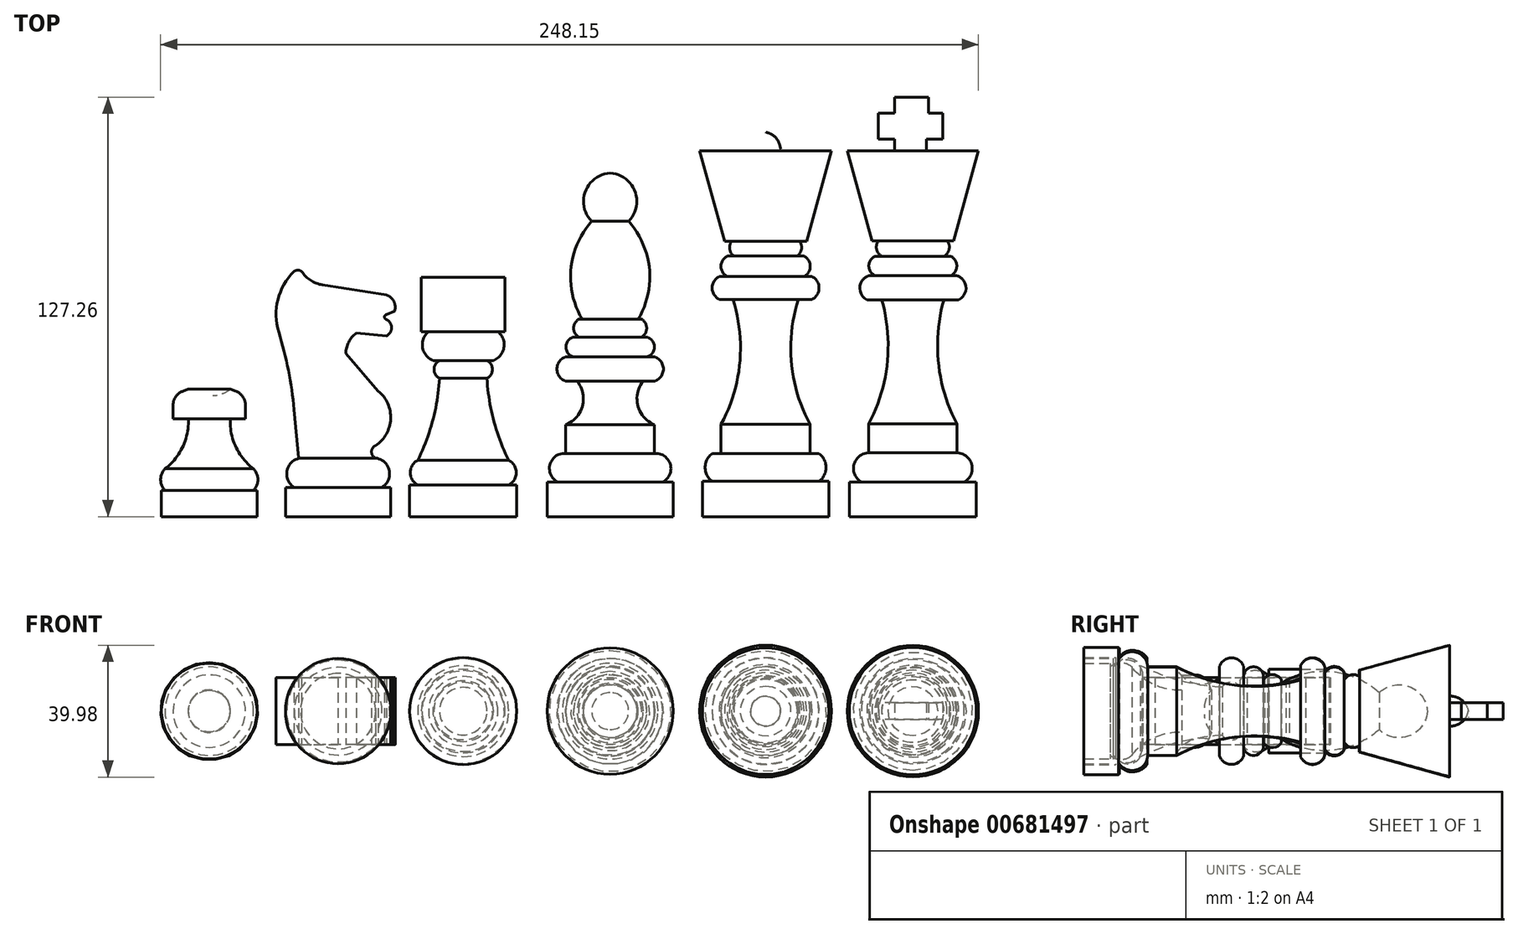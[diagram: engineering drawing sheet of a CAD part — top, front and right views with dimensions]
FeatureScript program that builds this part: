
annotation { "Feature Type Name" : "Feature", "Feature Type Description" : "" }
export const myFeature = defineFeature(function(context is Context, id is Id, definition is map)
    precondition{}
    {
        {
            var Q0;
            Q0=qCreatedBy(makeId("Top.planeOp"),FACE);
            var sketch = newSketch(context, id + "F0", { "sketchPlane" : qUnion([Q0])});
            skLineSegment(sketch, "E0", {"start": v(0, 0) * mm, "end": v(0, 127.26) * mm});
            skLineSegment(sketch, "E1", {"start": v(0, 0) * mm, "end": v(19.3, 0) * mm});
            skLineSegment(sketch, "E2", {"start": v(19.3, 0) * mm, "end": v(19.3, 10.5) * mm});
            skLineSegment(sketch, "E3", {"start": v(19.3, 10.5) * mm, "end": v(15.6, 10.5) * mm});
            skLineSegment(sketch, "E4", {"start": v(13.4, 19.39) * mm, "end": v(13.4, 28.12) * mm});
            skArc(sketch, "E5", {"start": v(9.43, 65.79) * mm, "mid": v(7.78, 46.57) * mm, "end": v(13.4, 28.12) * mm});
            skLineSegment(sketch, "E6", {"start": v(9.43, 65.79) * mm, "end": v(13.93, 65.79) * mm});
            skArc(sketch, "E7", {"start": v(13.93, 65.79) * mm, "mid": v(16.1, 69.74) * mm, "end": v(13.14, 73.14) * mm});
            skLineSegment(sketch, "E8", {"start": v(13.14, 73.14) * mm, "end": v(11.52, 73.14) * mm});
            skArc(sketch, "E9", {"start": v(11.52, 73.14) * mm, "mid": v(13.36, 76.06) * mm, "end": v(11.52, 78.98) * mm});
            skLineSegment(sketch, "E10", {"start": v(11.52, 78.98) * mm, "end": v(9.46, 78.98) * mm});
            skArc(sketch, "E11", {"start": v(9.46, 78.98) * mm, "mid": v(11.01, 81.12) * mm, "end": v(10.4, 83.7) * mm});
            skLineSegment(sketch, "E12", {"start": v(10.4, 83.7) * mm, "end": v(12.4, 83.7) * mm});
            skLineSegment(sketch, "E13", {"start": v(12.4, 83.7) * mm, "end": v(19.92, 110.96) * mm});
            skLineSegment(sketch, "E14", {"start": v(4.77, 127.26) * mm, "end": v(-5.47, 127.26) * mm});
            skLineSegment(sketch, "E15", {"start": v(19.92, 110.96) * mm, "end": v(0, 110.96) * mm});
            skArc(sketch, "E16", {"start": v(15.6, 10.5) * mm, "mid": v(17.9, 15.67) * mm, "end": v(13.6, 19.37) * mm});
            skLineSegment(sketch, "E17", {"start": v(13.4, 19.39) * mm, "end": v(13.6, 19.37) * mm});
            skLineSegment(sketch, "E18", {"start": v(0, 110.96) * mm, "end": v(0, 0) * mm});
            skLineSegment(sketch, "E19", {"start": v(0, 110.96) * mm, "end": v(0, 127.26) * mm});
            skLineSegment(sketch, "E20", {"start": v(4.77, 127.26) * mm, "end": v(4.77, 122.37) * mm});
            skLineSegment(sketch, "E21", {"start": v(4.77, 122.37) * mm, "end": v(9.1, 122.37) * mm});
            skLineSegment(sketch, "E22", {"start": v(9.1, 122.37) * mm, "end": v(9.1, 114.55) * mm});
            skLineSegment(sketch, "E23", {"start": v(9.1, 114.55) * mm, "end": v(4.14, 114.55) * mm});
            skLineSegment(sketch, "E24", {"start": v(4.14, 114.55) * mm, "end": v(4.14, 110.96) * mm});
            skLineSegment(sketch, "E25", {"start": v(-5.47, 127.26) * mm, "end": v(-5.47, 122.37) * mm});
            skLineSegment(sketch, "E26", {"start": v(-5.47, 122.37) * mm, "end": v(-10.42, 122.37) * mm});
            skLineSegment(sketch, "E27", {"start": v(-10.42, 122.37) * mm, "end": v(-10.42, 114.55) * mm});
            skLineSegment(sketch, "E28", {"start": v(-10.42, 114.55) * mm, "end": v(-5.47, 114.55) * mm});
            skLineSegment(sketch, "E29", {"start": v(-5.47, 114.55) * mm, "end": v(-5.47, 110.96) * mm});
            skLineSegment(sketch, "E30", {"start": v(-5.47, 110.96) * mm, "end": v(0, 110.96) * mm});
            skLineSegment(sketch, "E31", {"start": v(-44.68, 0) * mm, "end": v(-25.47, 0) * mm});
            skLineSegment(sketch, "E32", {"start": v(-25.47, 0) * mm, "end": v(-25.47, 10.69) * mm});
            skLineSegment(sketch, "E33", {"start": v(-25.47, 10.69) * mm, "end": v(-28.51, 10.69) * mm});
            skArc(sketch, "E34", {"start": v(-28.51, 10.69) * mm, "mid": v(-26.34, 14.92) * mm, "end": v(-28.51, 19.15) * mm});
            skLineSegment(sketch, "E35", {"start": v(-28.51, 19.15) * mm, "end": v(-31.18, 19.15) * mm});
            skLineSegment(sketch, "E36", {"start": v(-31.18, 19.15) * mm, "end": v(-31.18, 28.02) * mm});
            skArc(sketch, "E37", {"start": v(-34.78, 65.9) * mm, "mid": v(-36.84, 46.6) * mm, "end": v(-31.18, 28.02) * mm});
            skLineSegment(sketch, "E38", {"start": v(-34.78, 65.9) * mm, "end": v(-30.58, 65.9) * mm});
            skArc(sketch, "E39", {"start": v(-30.58, 65.9) * mm, "mid": v(-28.47, 69.37) * mm, "end": v(-30.58, 72.84) * mm});
            skLineSegment(sketch, "E40", {"start": v(-30.58, 72.84) * mm, "end": v(-33.03, 72.84) * mm});
            skArc(sketch, "E41", {"start": v(-33.03, 72.84) * mm, "mid": v(-31.13, 75.93) * mm, "end": v(-33.03, 79.02) * mm});
            skLineSegment(sketch, "E42", {"start": v(-33.03, 79.02) * mm, "end": v(-35.05, 79.02) * mm});
            skArc(sketch, "E43", {"start": v(-35.05, 79.02) * mm, "mid": v(-33.8, 81.1) * mm, "end": v(-34.32, 83.47) * mm});
            skLineSegment(sketch, "E44", {"start": v(-34.32, 83.47) * mm, "end": v(-32.26, 83.47) * mm});
            skLineSegment(sketch, "E45", {"start": v(-32.26, 83.47) * mm, "end": v(-24.7, 110.92) * mm});
            skLineSegment(sketch, "E46", {"start": v(-24.7, 110.92) * mm, "end": v(-44.68, 110.92) * mm});
            skLineSegment(sketch, "E47", {"start": v(-44.68, 110.92) * mm, "end": v(-44.68, 0) * mm});
            skLineSegment(sketch, "E48", {"start": v(-44.68, 110.92) * mm, "end": v(-44.68, 116.61) * mm});
            skArc(sketch, "E49", {"start": v(-40.14, 110.92) * mm, "mid": v(-41.33, 114.62) * mm, "end": v(-44.68, 116.61) * mm});
            skLineSegment(sketch, "E50", {"start": v(-91.84, 0) * mm, "end": v(-72.7, 0) * mm});
            skLineSegment(sketch, "E51", {"start": v(-72.7, 0) * mm, "end": v(-72.7, 10.5) * mm});
            skLineSegment(sketch, "E52", {"start": v(-72.7, 10.5) * mm, "end": v(-75.93, 10.5) * mm});
            skArc(sketch, "E53", {"start": v(-75.93, 10.5) * mm, "mid": v(-73.47, 15.34) * mm, "end": v(-77.33, 19.15) * mm});
            skLineSegment(sketch, "E54", {"start": v(-77.33, 19.15) * mm, "end": v(-78.38, 19.15) * mm});
            skLineSegment(sketch, "E55", {"start": v(-78.38, 19.15) * mm, "end": v(-78.38, 27.88) * mm});
            skArc(sketch, "E56", {"start": v(-81.78, 41.15) * mm, "mid": v(-83.44, 33.65) * mm, "end": v(-78.38, 27.88) * mm});
            skLineSegment(sketch, "E57", {"start": v(-81.78, 41.15) * mm, "end": v(-78.22, 41.15) * mm});
            skArc(sketch, "E58", {"start": v(-78.22, 41.15) * mm, "mid": v(-75.7, 44.8) * mm, "end": v(-78.22, 48.43) * mm});
            skLineSegment(sketch, "E59", {"start": v(-78.22, 48.43) * mm, "end": v(-80.75, 48.43) * mm});
            skArc(sketch, "E60", {"start": v(-80.75, 48.43) * mm, "mid": v(-78.41, 51.46) * mm, "end": v(-80.75, 54.48) * mm});
            skLineSegment(sketch, "E61", {"start": v(-80.75, 54.48) * mm, "end": v(-82.28, 54.48) * mm});
            skArc(sketch, "E62", {"start": v(-82.28, 54.48) * mm, "mid": v(-80.76, 57.18) * mm, "end": v(-82.28, 59.87) * mm});
            skLineSegment(sketch, "E63", {"start": v(-82.28, 59.87) * mm, "end": v(-83.35, 59.87) * mm});
            skArc(sketch, "E64", {"start": v(-83.35, 59.87) * mm, "mid": v(-79.94, 75.2) * mm, "end": v(-86.24, 89.57) * mm});
            skArc(sketch, "E65", {"start": v(-86.24, 89.57) * mm, "mid": v(-84.33, 98.68) * mm, "end": v(-91.84, 104.19) * mm});
            skLineSegment(sketch, "E66", {"start": v(-91.84, 104.19) * mm, "end": v(-91.84, 0) * mm});
            skLineSegment(sketch, "E67", {"start": v(-136.43, 0) * mm, "end": v(-120.2, 0) * mm});
            skLineSegment(sketch, "E68", {"start": v(-120.2, 0) * mm, "end": v(-120.2, 9.62) * mm});
            skLineSegment(sketch, "E69", {"start": v(-120.2, 9.62) * mm, "end": v(-122.64, 9.62) * mm});
            skArc(sketch, "E70", {"start": v(-122.64, 9.62) * mm, "mid": v(-120.34, 13.36) * mm, "end": v(-122.64, 17.1) * mm});
            skArc(sketch, "E71", {"start": v(-129.21, 41.96) * mm, "mid": v(-127.2, 29.2) * mm, "end": v(-122.64, 17.1) * mm});
            skArc(sketch, "E72", {"start": v(-129.21, 41.96) * mm, "mid": v(-127.57, 44.66) * mm, "end": v(-129.21, 47.37) * mm});
            skLineSegment(sketch, "E73", {"start": v(-129.21, 47.37) * mm, "end": v(-127.23, 47.37) * mm});
            skArc(sketch, "E74", {"start": v(-127.23, 47.37) * mm, "mid": v(-124.06, 51.37) * mm, "end": v(-125.93, 56.12) * mm});
            skLineSegment(sketch, "E75", {"start": v(-125.93, 56.12) * mm, "end": v(-123.74, 56.12) * mm});
            skLineSegment(sketch, "E76", {"start": v(-123.74, 56.12) * mm, "end": v(-123.74, 72.64) * mm});
            skLineSegment(sketch, "E77", {"start": v(-123.74, 72.64) * mm, "end": v(-136.43, 72.64) * mm});
            skLineSegment(sketch, "E78", {"start": v(-136.43, 72.64) * mm, "end": v(-136.43, 0) * mm});
            skLineSegment(sketch, "E79", {"start": v(-213.48, 0) * mm, "end": v(-199, 0) * mm});
            skLineSegment(sketch, "E80", {"start": v(-199, 0) * mm, "end": v(-199, 7.95) * mm});
            skLineSegment(sketch, "E81", {"start": v(-199, 7.95) * mm, "end": v(-200.07, 7.95) * mm});
            skArc(sketch, "E82", {"start": v(-200.07, 7.95) * mm, "mid": v(-198.73, 11.23) * mm, "end": v(-200.07, 14.51) * mm});
            skArc(sketch, "E83", {"start": v(-207.12, 29.7) * mm, "mid": v(-205.47, 21.24) * mm, "end": v(-200.07, 14.51) * mm});
            skLineSegment(sketch, "E84", {"start": v(-207.12, 29.7) * mm, "end": v(-202.5, 29.7) * mm});
            skLineSegment(sketch, "E85", {"start": v(-202.5, 29.7) * mm, "end": v(-202.5, 33.78) * mm});
            skArc(sketch, "E86", {"start": v(-202.5, 33.78) * mm, "mid": v(-203.31, 36.39) * mm, "end": v(-205.47, 38.07) * mm});
            skLineSegment(sketch, "E87", {"start": v(-205.47, 38.07) * mm, "end": v(-207.05, 38.66) * mm});
            skArc(sketch, "E88", {"start": v(-207.05, 38.66) * mm, "mid": v(-204.14, 49.4) * mm, "end": v(-213.48, 55.46) * mm});
            skLineSegment(sketch, "E89", {"start": v(-213.48, 55.46) * mm, "end": v(-213.48, 0) * mm});
            skLineSegment(sketch, "E90", {"start": v(-174.39, 0) * mm, "end": v(-158.4, 0) * mm});
            skLineSegment(sketch, "E91", {"start": v(-158.4, 0) * mm, "end": v(-158.4, 8.9) * mm});
            skLineSegment(sketch, "E92", {"start": v(-158.4, 8.9) * mm, "end": v(-161.1, 8.9) * mm});
            skArc(sketch, "E93", {"start": v(-161.1, 8.9) * mm, "mid": v(-158.89, 14) * mm, "end": v(-162.97, 17.77) * mm});
            skLineSegment(sketch, "E94", {"start": v(-162.97, 17.77) * mm, "end": v(-174.39, 17.77) * mm});
            skLineSegment(sketch, "E95", {"start": v(-174.39, 17.77) * mm, "end": v(-174.39, 0) * mm});
            skArc(sketch, "E96", {"start": v(-162.97, 21.59) * mm, "mid": v(-164.25, 19.68) * mm, "end": v(-162.97, 17.77) * mm});
            skArc(sketch, "E97", {"start": v(-162.97, 21.59) * mm, "mid": v(-158.46, 29.65) * mm, "end": v(-162.2, 38.1) * mm});
            skLineSegment(sketch, "E98", {"start": v(-162.2, 38.1) * mm, "end": v(-172.04, 49.47) * mm});
            skArc(sketch, "E99", {"start": v(-168.89, 55.65) * mm, "mid": v(-171.2, 52.93) * mm, "end": v(-172.04, 49.47) * mm});
            skLineSegment(sketch, "E100", {"start": v(-168.89, 55.65) * mm, "end": v(-159.67, 54.86) * mm});
            skArc(sketch, "E101", {"start": v(-159.67, 54.86) * mm, "mid": v(-158.17, 57.31) * mm, "end": v(-159.67, 59.76) * mm});
            skArc(sketch, "E102", {"start": v(-159.67, 61.33) * mm, "mid": v(-160.33, 60.55) * mm, "end": v(-159.67, 59.76) * mm});
            skLineSegment(sketch, "E103", {"start": v(-159.67, 61.33) * mm, "end": v(-157.26, 62.3) * mm});
            skArc(sketch, "E104", {"start": v(-157.26, 62.3) * mm, "mid": v(-157.47, 65.3) * mm, "end": v(-159.75, 67.24) * mm});
            skLineSegment(sketch, "E105", {"start": v(-159.75, 67.24) * mm, "end": v(-179.11, 70.29) * mm});
            skArc(sketch, "E106", {"start": v(-185.45, 74.34) * mm, "mid": v(-182.7, 71.65) * mm, "end": v(-179.11, 70.29) * mm});
            skArc(sketch, "E107", {"start": v(-185.45, 74.34) * mm, "mid": v(-186.6, 74.76) * mm, "end": v(-187.73, 74.34) * mm});
            skArc(sketch, "E108", {"start": v(-187.73, 74.34) * mm, "mid": v(-192.67, 65.82) * mm, "end": v(-192.4, 55.97) * mm});
            skArc(sketch, "E109", {"start": v(-187.73, 32.46) * mm, "mid": v(-189.45, 44.34) * mm, "end": v(-192.4, 55.97) * mm});
            skLineSegment(sketch, "E110", {"start": v(-187.73, 32.46) * mm, "end": v(-186.4, 17.8) * mm});
            skLineSegment(sketch, "E111", {"start": v(-186.4, 17.8) * mm, "end": v(-174.39, 17.77) * mm});
            skSolve(sketch);
        }
        {
            var Q0;
            {var subQ0=sQuery(id+"F0.wireOp",EDGE,"E1");Q0=makeQuery(id+"F0.imprint","IMPRINT",FACE,{"disambiguationData":[TD([[makeQuery(id+"F0.imprint","IMPRINT",EDGE,{"derivedFrom":subQ0}),1.0]])]});}
            var Q1;
            Q1=sQuery(id+"F0.wireOp",EDGE,"E0");
            revolve(context, id + "F1", {"entities" : qUnion([Q0]), "axis" : qUnion([Q1]), "revolveType" : RevolveType.FULL});
        }
        {
            var Q0;
            {var subQ3=sQuery(id+"F0.wireOp",EDGE,"E25");Q0=makeQuery(id+"F0.imprint","IMPRINT",FACE,{"disambiguationData":[TD([[makeQuery(id+"F0.imprint","IMPRINT",EDGE,{"derivedFrom":subQ3}),1.0]])]});}
            var Q1;
            {var subQ4=sQuery(id+"F0.wireOp",EDGE,"E20");Q1=makeQuery(id+"F0.imprint","IMPRINT",FACE,{"disambiguationData":[TD([[makeQuery(id+"F0.imprint","IMPRINT",EDGE,{"derivedFrom":subQ4}),-1.0]])]});}
            extrude(context, id + "F2", {"entities" : qUnion([Q0, Q1]), "operationType" : NewBodyOperationType.ADD, "endBound" : BoundingType.SYMMETRIC, "depth" : 5.08 * mm, "offsetDistance" : 25.4 * mm});
        }
        {
            var Q0;
            Q0=makeQuery(id+"F0.imprint","IMPRINT",FACE,{"disambiguationData":[TD([[makeQuery(id+"F0.imprint","IMPRINT",EDGE,{"derivedFrom":sQuery(id+"F0.wireOp",EDGE,"E31")}),1.0]])]});
            var Q1;
            Q1=sQuery(id+"F0.wireOp",EDGE,"E47");
            revolve(context, id + "F3", {"entities" : qUnion([Q0]), "axis" : qUnion([Q1]), "revolveType" : RevolveType.FULL});
        }
        {
            var Q0;
            {var subQ0=sQuery(id+"F0.wireOp",EDGE,"E48");Q0=makeQuery(id+"F0.imprint","IMPRINT",FACE,{"disambiguationData":[TD([[makeQuery(id+"F0.imprint","IMPRINT",EDGE,{"derivedFrom":subQ0}),-1.0]])]});}
            var Q1;
            Q1=sQuery(id+"F0.wireOp",EDGE,"E48");
            revolve(context, id + "F4", {"operationType" : NewBodyOperationType.ADD, "entities" : qUnion([Q0]), "axis" : qUnion([Q1]), "revolveType" : RevolveType.FULL});
        }
        {
            var Q0;
            Q0=makeQuery(id+"F0.imprint","IMPRINT",FACE,{"disambiguationData":[TD([[makeQuery(id+"F0.imprint","IMPRINT",EDGE,{"derivedFrom":sQuery(id+"F0.wireOp",EDGE,"E50")}),1.0]])]});
            var Q1;
            Q1=sQuery(id+"F0.wireOp",EDGE,"E66");
            revolve(context, id + "F5", {"entities" : qUnion([Q0]), "axis" : qUnion([Q1]), "revolveType" : RevolveType.FULL});
        }
        {
            var Q0;
            Q0=makeQuery(id+"F0.imprint","IMPRINT",FACE,{"disambiguationData":[TD([[makeQuery(id+"F0.imprint","IMPRINT",EDGE,{"derivedFrom":sQuery(id+"F0.wireOp",EDGE,"E67")}),1.0]])]});
            var Q1;
            Q1=sQuery(id+"F0.wireOp",EDGE,"E78");
            revolve(context, id + "F6", {"surfaceOperationType" : NewSurfaceOperationType.NEW, "entities" : qUnion([Q0]), "axis" : qUnion([Q1]), "revolveType" : RevolveType.FULL});
        }
        {
            var Q0;
            Q0=makeQuery(id+"F0.imprint","IMPRINT",FACE,{"disambiguationData":[TD([[makeQuery(id+"F0.imprint","IMPRINT",EDGE,{"derivedFrom":sQuery(id+"F0.wireOp",EDGE,"E79")}),1.0]])]});
            var Q1;
            Q1=sQuery(id+"F0.wireOp",EDGE,"E89");
            revolve(context, id + "F7", {"surfaceOperationType" : NewSurfaceOperationType.NEW, "entities" : qUnion([Q0]), "axis" : qUnion([Q1]), "revolveType" : RevolveType.FULL});
        }
        {
            var Q0;
            Q0=makeQuery(id+"F0.imprint","IMPRINT",FACE,{"disambiguationData":[TD([[makeQuery(id+"F0.imprint","IMPRINT",EDGE,{"derivedFrom":sQuery(id+"F0.wireOp",EDGE,"E90")}),1.0]])]});
            var Q1;
            Q1=sQuery(id+"F0.wireOp",EDGE,"E95");
            revolve(context, id + "F8", {"surfaceOperationType" : NewSurfaceOperationType.NEW, "entities" : qUnion([Q0]), "axis" : qUnion([Q1]), "revolveType" : RevolveType.FULL});
        }
        {
            var Q0;
            Q0=makeQuery(id+"F0.imprint","IMPRINT",FACE,{"disambiguationData":[TD([[makeQuery(id+"F0.imprint","IMPRINT",EDGE,{"derivedFrom":sQuery(id+"F0.wireOp",EDGE,"E94")}),-1.0]])]});
            extrude(context, id + "F9", {"entities" : qUnion([Q0]), "operationType" : NewBodyOperationType.ADD, "endBound" : BoundingType.SYMMETRIC, "depth" : 20.32 * mm, "offsetDistance" : 25.4 * mm});
        }
    });
